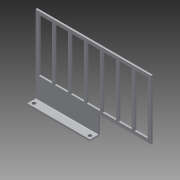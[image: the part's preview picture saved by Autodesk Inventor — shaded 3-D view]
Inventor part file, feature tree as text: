
AUTODESK INVENTOR PART (.ipt)
format: ipt  version: 2013 (Build 170138000, 138)  size: 233,984 bytes
history: native  units: in
note: dims shown in document units (in); Inventor stores cm internally (conversion verified against a paired STEP export)
features: sheet_metal_op x6, other x5, sketch x3
ambient origin geometry x8: Origin, YZ Plane, XZ Plane, XY Plane, X Axis, Y Axis, Z Axis, Center Point
bodies: Solid1 (feature_tree)
feature tree (14):
  sheet_metal_op  "Face1"
  sheet_metal_op  "Flange1"
  sheet_metal_op  "Face2"
  sketch  "Sketch1"  dims[d0=0.75in]
  other  "Plate1"
  sketch  "Sketch2"  dims[d1=4.75in]
  other  "Plate2"
  sheet_metal_op  "Bend1"
  sheet_metal_op  "Corner1"
  other  "Plate3"
  sheet_metal_op  "Bend2"
  sketch  "Sketch5"  dims[d2=0.266in d3=0.266in d4=4.25in d5=0.25in d6=0.5in d7=0.5in d8=0.125in d9=0.125in d10=0.0625in d11=0.25in d12=0.125in d13=1.5in d14=90.0deg d15=0.05in d16=0.5in d17=0.125in d18=0.125in d21=0.125in d22=0.125in d23=0.0625in d24=0.25in d25=0.125in d42=2.5in d43=4.0in d44=2.0in d45=1.0in d46=0.25in d47=0.25in d48=2.7559in d50=1.2083in d51=0.3937in d53=1.0in d55=0.125in d56=0.0in]
  other  "Cut2"
  other  "Definition1"
